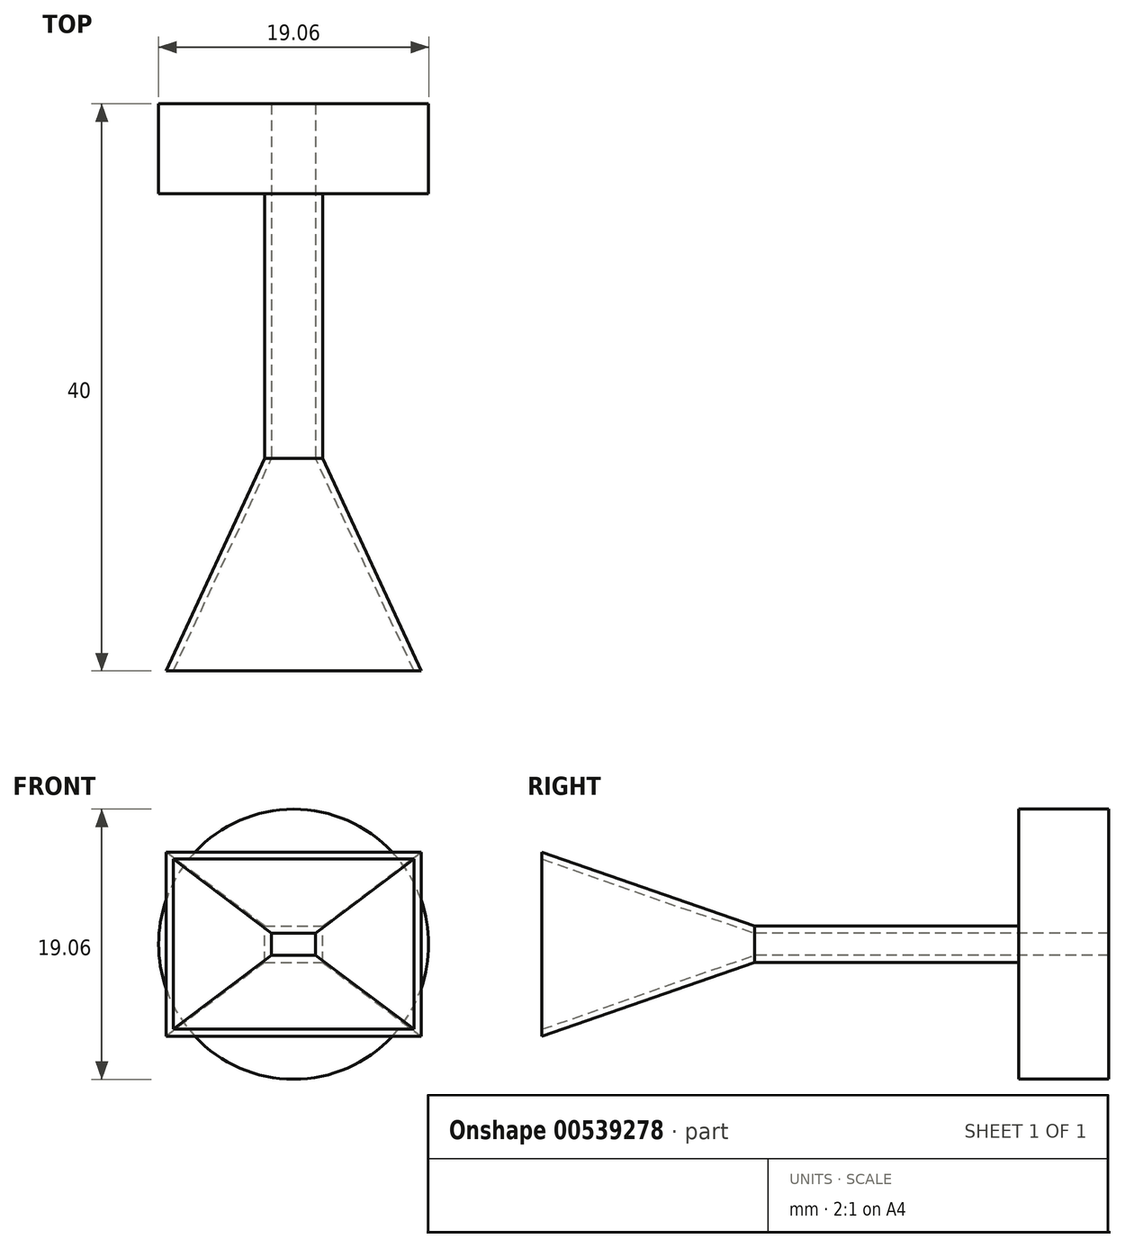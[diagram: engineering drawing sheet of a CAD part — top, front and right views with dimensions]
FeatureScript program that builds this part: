
annotation { "Feature Type Name" : "Feature", "Feature Type Description" : "" }
export const myFeature = defineFeature(function(context is Context, id is Id, definition is map)
    precondition{}
    {
        {
            var Q0;
            Q0=qCreatedBy(makeId("Front.planeOp"),FACE);
            var sketch = newSketch(context, id + "F0", { "sketchPlane" : qUnion([Q0])});
            skPoint(sketch, "E0.middle", {"position": v(0, 0) * mm});
            skLineSegment(sketch, "E1.bottom", {"start": v(-2.05, -1.27) * mm, "end": v(2.05, -1.27) * mm});
            skLineSegment(sketch, "E1.top", {"start": v(-2.05, 1.27) * mm, "end": v(2.05, 1.27) * mm});
            skLineSegment(sketch, "E1.left", {"start": v(-2.05, -1.27) * mm, "end": v(-2.05, 1.27) * mm});
            skLineSegment(sketch, "E1.right", {"start": v(2.05, -1.27) * mm, "end": v(2.05, 1.27) * mm});
            skSolve(sketch);
        }
        {
            var Q0;
            Q0=qCreatedBy(makeId("Front.planeOp"),FACE);
            cPlane(context, id + "F1", {"entities" : qUnion([Q0]), "cplaneType" : CPlaneType.OFFSET, "offset" : 15 * mm, "width" : 150 * mm, "height" : 150 * mm});
        }
        {
            var Q0;
            Q0=qCreatedBy(id+"F1.planeOp",FACE);
            var sketch = newSketch(context, id + "F2", { "sketchPlane" : qUnion([Q0])});
            skLineSegment(sketch, "E2.bottom", {"start": v(-9, 6.5) * mm, "end": v(9, 6.5) * mm});
            skLineSegment(sketch, "E2.top", {"start": v(-9, -6.5) * mm, "end": v(9, -6.5) * mm});
            skLineSegment(sketch, "E2.left", {"start": v(-9, 6.5) * mm, "end": v(-9, -6.5) * mm});
            skLineSegment(sketch, "E2.right", {"start": v(9, 6.5) * mm, "end": v(9, -6.5) * mm});
            skPoint(sketch, "E2.middle", {"position": v(0, 0) * mm});
            skSolve(sketch);
        }
        {
            var Q0;
            Q0=qCreatedBy(id+"F1.planeOp",FACE);
            var sketch = newSketch(context, id + "F3", { "sketchPlane" : qUnion([Q0])});
            skLineSegment(sketch, "E3.bottom", {"start": v(-8.5, -6) * mm, "end": v(8.5, -6) * mm});
            skLineSegment(sketch, "E3.top", {"start": v(-8.5, 6) * mm, "end": v(8.5, 6) * mm});
            skLineSegment(sketch, "E3.left", {"start": v(-8.5, -6) * mm, "end": v(-8.5, 6) * mm});
            skLineSegment(sketch, "E3.right", {"start": v(8.5, -6) * mm, "end": v(8.5, 6) * mm});
            skPoint(sketch, "E3.middle", {"position": v(0, 0) * mm});
            skSolve(sketch);
        }
        {
            var Q0;
            Q0=qCreatedBy(makeId("Front.planeOp"),FACE);
            var sketch = newSketch(context, id + "F4", { "sketchPlane" : qUnion([Q0])});
            skLineSegment(sketch, "E4.bottom", {"start": v(-1.55, 0.78) * mm, "end": v(1.55, 0.78) * mm});
            skLineSegment(sketch, "E4.top", {"start": v(-1.55, -0.78) * mm, "end": v(1.55, -0.78) * mm});
            skLineSegment(sketch, "E4.left", {"start": v(-1.55, 0.78) * mm, "end": v(-1.55, -0.78) * mm});
            skLineSegment(sketch, "E4.right", {"start": v(1.55, 0.78) * mm, "end": v(1.55, -0.78) * mm});
            skPoint(sketch, "E4.middle", {"position": v(0, 0) * mm});
            skSolve(sketch);
        }
        {
            var Q0;
            Q0=makeQuery(id+"F0.imprint","IMPRINT",FACE,{"disambiguationData":[TD([[makeQuery(id+"F0.imprint","IMPRINT",EDGE,{"derivedFrom":sQuery(id+"F0.wireOp",EDGE,"E1.bottom")}),1.0]])]});
            var Q1;
            Q1=makeQuery(id+"F2.imprint","IMPRINT",FACE,{"disambiguationData":[TD([[makeQuery(id+"F2.imprint","IMPRINT",EDGE,{"derivedFrom":sQuery(id+"F2.wireOp",EDGE,"E2.bottom")}),-1.0]])]});
            loft(context, id + "F5", {"sheetProfilesArray" : [{ "sheetProfileEntities" : qUnion([Q0]) }, { "sheetProfileEntities" : qUnion([Q1]) }]});
        }
        {
            var Q1;
            Q1=makeQuery(id+"F3.imprint","IMPRINT",FACE,{"disambiguationData":[TD([[makeQuery(id+"F3.imprint","IMPRINT",EDGE,{"derivedFrom":sQuery(id+"F3.wireOp",EDGE,"E3.bottom")}),1.0]])]});
            var Q2;
            Q2=makeQuery(id+"F4.imprint","IMPRINT",FACE,{"disambiguationData":[TD([[makeQuery(id+"F4.imprint","IMPRINT",EDGE,{"derivedFrom":sQuery(id+"F4.wireOp",EDGE,"E4.bottom")}),-1.0]])]});
            loft(context, id + "F6", {"operationType" : NewBodyOperationType.REMOVE, "sheetProfilesArray" : [{ "sheetProfileEntities" : qUnion([Q1]) }, { "sheetProfileEntities" : qUnion([Q2]) }]});
        }
        {
            var Q0;
            Q0=makeQuery(id+"F5.opLoft","CAP_FACE",FACE,{"disambiguationData":[OSD([makeQuery(id+"F0.imprint","IMPRINT",FACE,{"disambiguationData":[TD([[makeQuery(id+"F0.imprint","IMPRINT",EDGE,{"derivedFrom":sQuery(id+"F0.wireOp",EDGE,"E1.bottom")}),1.0]])]})])],"isStart":true});
            extrude(context, id + "F7", {"entities" : qUnion([Q0]), "operationType" : NewBodyOperationType.ADD, "depth" : 25 * mm, "offsetDistance" : 25 * mm});
        }
        {
            var Q0;
            Q0=makeQuery(id+"F7.opExtrude","CAP_FACE",FACE,{"disambiguationData":[OSD([makeQuery(id+"F0.imprint","IMPRINT",FACE,{"disambiguationData":[TD([[makeQuery(id+"F0.imprint","IMPRINT",EDGE,{"derivedFrom":sQuery(id+"F0.wireOp",EDGE,"E1.bottom")}),1.0]])]})])],"isStart":false});
            var sketch = newSketch(context, id + "F8", { "sketchPlane" : qUnion([Q0])});
            skCircle(sketch, "E5", {"center": v(0, 0) * mm, "radius": 9.53 * mm});
            skSolve(sketch);
        }
        {
            var Q0;
            Q0=makeQuery(id+"F8.imprint","IMPRINT",FACE,{"disambiguationData":[TD([[makeQuery(id+"F8.imprint","IMPRINT",EDGE,{"derivedFrom":sQuery(id+"F8.wireOp",EDGE,"E5")}),1.0]])]});
            extrude(context, id + "F9", {"entities" : qUnion([Q0]), "operationType" : NewBodyOperationType.ADD, "oppositeDirection" : true, "depth" : 6.35 * mm, "offsetDistance" : 25 * mm});
        }
    });
